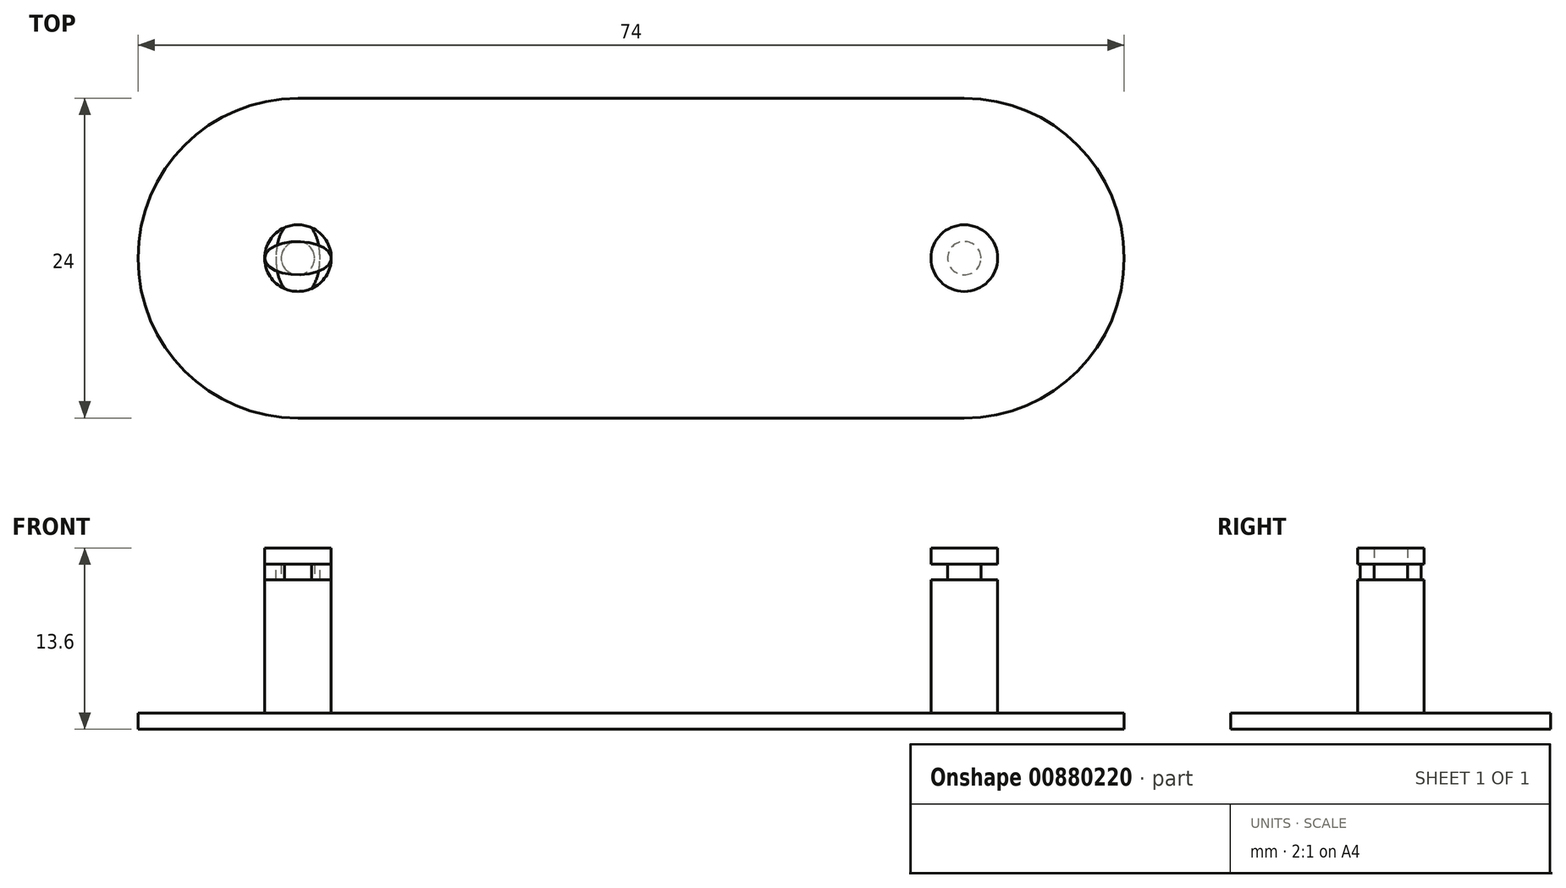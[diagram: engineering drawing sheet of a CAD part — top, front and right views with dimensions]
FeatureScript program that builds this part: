
annotation { "Feature Type Name" : "Feature", "Feature Type Description" : "" }
export const myFeature = defineFeature(function(context is Context, id is Id, definition is map)
    precondition{}
    {
        {
            var Q0;
            Q0=qCreatedBy(makeId("Top.planeOp"),FACE);
            var sketch = newSketch(context, id + "F0", { "sketchPlane" : qUnion([Q0])});
            skLineSegment(sketch, "E0", {"start": v(0, -12) * mm, "end": v(50, -12) * mm});
            skLineSegment(sketch, "E1", {"start": v(0, 12) * mm, "end": v(50, 12) * mm});
            skArc(sketch, "E2", {"start": v(0, -12) * mm, "mid": v(-12, 0) * mm, "end": v(0, 12) * mm});
            skArc(sketch, "E3", {"start": v(50, 12) * mm, "mid": v(62, 0) * mm, "end": v(50, -12) * mm});
            skSolve(sketch);
        }
        {
            var Q0;
            Q0=makeQuery(id+"F0.imprint","IMPRINT",FACE,{"disambiguationData":[TD([[makeQuery(id+"F0.imprint","IMPRINT",EDGE,{"derivedFrom":sQuery(id+"F0.wireOp",EDGE,"E0")}),1.0]])]});
            extrude(context, id + "F1", {"entities" : qUnion([Q0]), "depth" : 1.2 * mm, "offsetDistance" : 25 * mm});
        }
        {
            var Q0;
            Q0=makeQuery(id+"F1.opExtrude","CAP_FACE",FACE,{"disambiguationData":[OSD([sQuery(id+"F0.wireOp",EDGE,"E0"),sQuery(id+"F0.wireOp",EDGE,"E1"),sQuery(id+"F0.wireOp",EDGE,"E2"),sQuery(id+"F0.wireOp",EDGE,"E3")])],"isStart":false});
            var sketch = newSketch(context, id + "F2", { "sketchPlane" : qUnion([Q0])});
            skCircle(sketch, "E4", {"center": v(0, 0) * mm, "radius": 2.5 * mm});
            skCircle(sketch, "E5", {"center": v(50, 0) * mm, "radius": 2.5 * mm});
            skSolve(sketch);
        }
        {
            var Q0;
            Q0 = qSketchRegion(id + "F2", true);
            extrude(context, id + "F3", {"entities" : qUnion([Q0]), "operationType" : NewBodyOperationType.ADD, "depth" : 10 * mm, "offsetDistance" : 25 * mm});
        }
        {
            var Q0;
            Q0=makeQuery(id+"F3.opExtrude","CAP_FACE",FACE,{"disambiguationData":[OSD([sQuery(id+"F2.wireOp",EDGE,"E4")])],"isStart":false});
            var sketch = newSketch(context, id + "F4", { "sketchPlane" : qUnion([Q0])});
            skCircle(sketch, "E6", {"center": v(0, 0) * mm, "radius": 1.25 * mm});
            skSolve(sketch);
        }
        {
            var Q0;
            Q0=makeQuery(id+"F3.opExtrude","CAP_FACE",FACE,{"disambiguationData":[OSD([sQuery(id+"F2.wireOp",EDGE,"E5")])],"isStart":false});
            var sketch = newSketch(context, id + "F5", { "sketchPlane" : qUnion([Q0])});
            skCircle(sketch, "E7", {"center": v(50, 0) * mm, "radius": 1.25 * mm});
            skSolve(sketch);
        }
        {
            var Q0;
            Q0=makeQuery(id+"F4.imprint","IMPRINT",FACE,{"disambiguationData":[TD([[makeQuery(id+"F4.imprint","IMPRINT",EDGE,{"derivedFrom":sQuery(id+"F4.wireOp",EDGE,"E6")}),1.0]])]});
            var Q1;
            Q1=makeQuery(id+"F5.imprint","IMPRINT",FACE,{"disambiguationData":[TD([[makeQuery(id+"F5.imprint","IMPRINT",EDGE,{"derivedFrom":sQuery(id+"F5.wireOp",EDGE,"E7")}),1.0]])]});
            extrude(context, id + "F6", {"entities" : qUnion([Q0, Q1]), "operationType" : NewBodyOperationType.ADD, "depth" : 1.2 * mm, "offsetDistance" : 25 * mm});
        }
        {
            var Q0;
            Q0=makeQuery(id+"F6.opExtrude","CAP_FACE",FACE,{"disambiguationData":[OSD([sQuery(id+"F4.wireOp",EDGE,"E6")])],"isStart":false});
            var sketch = newSketch(context, id + "F7", { "sketchPlane" : qUnion([Q0])});
            skEllipse(sketch, "E8", {"center": v(0, 0) * mm, "majorRadius": 1.25 * mm, "minorRadius": 2.5 * mm, "majorAxis": v(0, 1)});
            skSolve(sketch);
        }
        {
            var Q0;
            Q0=makeQuery(id+"F6.opExtrude","CAP_FACE",FACE,{"disambiguationData":[OSD([sQuery(id+"F5.wireOp",EDGE,"E7")])],"isStart":false});
            var sketch = newSketch(context, id + "F8", { "sketchPlane" : qUnion([Q0])});
            skCircle(sketch, "E9", {"center": v(50, 0) * mm, "radius": 2.5 * mm});
            skSolve(sketch);
        }
        {
            var Q0;
            {var subQ0=sQuery(id+"F7.wireOp",EDGE,"E8");var subQ1=makeQuery(id+"F6.opExtrude","CAP_EDGE",EDGE,{"disambiguationData":[OSD([sQuery(id+"F4.wireOp",EDGE,"E6")])],"isStart":false});var subQ2=makeQuery(id+"F7.imprint","INTERSECT",VERTEX,{"disambiguationData":[OD(0.0)],"derivedFrom":[subQ1,subQ0]});Q0=makeQuery(id+"F7.imprint","IMPRINT",FACE,{"disambiguationData":[TD([[makeQuery(id+"F7.imprint","IMPRINT",EDGE,{"disambiguationData":[TD([[subQ2,1.0]])],"derivedFrom":subQ0}),1.0]])]});}
            var Q1;
            {var subQ0=sQuery(id+"F7.wireOp",EDGE,"E8");var subQ1=makeQuery(id+"F6.opExtrude","CAP_EDGE",EDGE,{"disambiguationData":[OSD([sQuery(id+"F4.wireOp",EDGE,"E6")])],"isStart":false});var subQ2=makeQuery(id+"F7.imprint","INTERSECT",VERTEX,{"disambiguationData":[OD(0.0)],"derivedFrom":[subQ1,subQ0]});Q1=makeQuery(id+"F7.imprint","IMPRINT",FACE,{"disambiguationData":[TD([[makeQuery(id+"F7.imprint","IMPRINT",EDGE,{"disambiguationData":[TD([[subQ2,-1.0]])],"derivedFrom":subQ1}),1.0]])]});}
            var Q2;
            {var subQ0=sQuery(id+"F7.wireOp",EDGE,"E8");var subQ1=makeQuery(id+"F6.opExtrude","CAP_EDGE",EDGE,{"disambiguationData":[OSD([sQuery(id+"F4.wireOp",EDGE,"E6")])],"isStart":false});var subQ2=makeQuery(id+"F7.imprint","INTERSECT",VERTEX,{"disambiguationData":[OD(0.0)],"derivedFrom":[subQ1,subQ0]});Q2=makeQuery(id+"F7.imprint","IMPRINT",FACE,{"disambiguationData":[TD([[makeQuery(id+"F7.imprint","IMPRINT",EDGE,{"disambiguationData":[TD([[subQ2,-1.0]])],"derivedFrom":subQ0}),1.0]])]});}
            var Q3;
            Q3=makeQuery(id+"F8.imprint","IMPRINT",FACE,{"disambiguationData":[TD([[makeQuery(id+"F8.imprint","IMPRINT",EDGE,{"derivedFrom":sQuery(id+"F8.wireOp",EDGE,"E9")}),1.0]])]});
            var Q4;
            Q4=makeQuery(id+"F8.imprint","IMPRINT",FACE,{"disambiguationData":[TD([[makeQuery(id+"F8.imprint","IMPRINT",EDGE,{"derivedFrom":makeQuery(id+"F6.opExtrude","CAP_EDGE",EDGE,{"disambiguationData":[OSD([sQuery(id+"F5.wireOp",EDGE,"E7")])],"isStart":false})}),1.0]])]});
            extrude(context, id + "F9", {"entities" : qUnion([Q0, Q1, Q2, Q3, Q4]), "operationType" : NewBodyOperationType.ADD, "depth" : 1.2 * mm, "offsetDistance" : 25 * mm});
        }
        {
            var Q0;
            Q0=makeQuery(id+"F3.opExtrude","CAP_FACE",FACE,{"disambiguationData":[OSD([sQuery(id+"F2.wireOp",EDGE,"E4")])],"isStart":false});
            var sketch = newSketch(context, id + "F10", { "sketchPlane" : qUnion([Q0])});
            skArc(sketch, "E10.0", {"start": v(0, -12) * mm, "mid": v(-12, 0) * mm, "end": v(0, 12) * mm});
            skLineSegment(sketch, "E11.0", {"start": v(0, -12) * mm, "end": v(50, -12) * mm});
            skEllipse(sketch, "E12", {"center": v(0, 0) * mm, "majorRadius": 1.65 * mm, "minorRadius": 2.9 * mm, "majorAxis": v(1, 0)});
            skArc(sketch, "E13", {"start": v(51.65, 0) * mm, "mid": v(51.3, 6.04) * mm, "end": v(50.24, 12) * mm});
            skArc(sketch, "E14", {"start": v(48.4, -0.4) * mm, "mid": v(50.2, -1.64) * mm, "end": v(51.65, 0) * mm});
            skLineSegment(sketch, "E15", {"start": v(0, 12) * mm, "end": v(46.94, 12) * mm});
            skArc(sketch, "E16", {"start": v(50, -12) * mm, "mid": v(62, -0.12) * mm, "end": v(50.24, 12) * mm});
            skCircle(sketch, "E17.0", {"center": v(50, 0) * mm, "radius": 1.25 * mm, "construction": true});
            skLineSegment(sketch, "E18", {"start": v(48.4, -0.4) * mm, "end": v(46, -0.4) * mm});
            skLineSegment(sketch, "E19", {"start": v(46, -0.4) * mm, "end": v(46, 7.94) * mm});
            skLineSegment(sketch, "E20", {"start": v(46, 7.94) * mm, "end": v(48.35, 0) * mm});
            skArc(sketch, "E21", {"start": v(48.35, 0) * mm, "mid": v(48.83, 1.17) * mm, "end": v(50, 1.65) * mm});
            skLineSegment(sketch, "E22", {"start": v(50, 1.65) * mm, "end": v(46.94, 12) * mm});
            skSolve(sketch);
        }
        {
            var Q0;
            {var subQ11=sQuery(id+"F10.wireOp",EDGE,"E10.0");Q0=makeQuery(id+"F10.imprint","IMPRINT",FACE,{"disambiguationData":[TD([[makeQuery(id+"F10.imprint","IMPRINT",EDGE,{"derivedFrom":subQ11}),-1.0]])]});}
            var Q1;
            {var subQ0=sQuery(id+"F10.wireOp",EDGE,"E12");var subQ1=makeQuery(id+"F3.opExtrude","CAP_EDGE",EDGE,{"disambiguationData":[OSD([sQuery(id+"F2.wireOp",EDGE,"E4")])],"isStart":false});var subQ2=makeQuery(id+"F10.imprint","INTERSECT",VERTEX,{"disambiguationData":[OD(2.0)],"derivedFrom":[subQ1,subQ0]});Q1=makeQuery(id+"F10.imprint","IMPRINT",FACE,{"disambiguationData":[TD([[makeQuery(id+"F10.imprint","IMPRINT",EDGE,{"disambiguationData":[TD([[subQ2,-1.0]])],"derivedFrom":subQ0}),-1.0]])]});}
            var Q2;
            {var subQ0=sQuery(id+"F10.wireOp",EDGE,"E12");var subQ1=makeQuery(id+"F3.opExtrude","CAP_EDGE",EDGE,{"disambiguationData":[OSD([sQuery(id+"F2.wireOp",EDGE,"E4")])],"isStart":false});var subQ2=makeQuery(id+"F10.imprint","INTERSECT",VERTEX,{"disambiguationData":[OD(0.0)],"derivedFrom":[subQ1,subQ0]});Q2=makeQuery(id+"F10.imprint","IMPRINT",FACE,{"disambiguationData":[TD([[makeQuery(id+"F10.imprint","IMPRINT",EDGE,{"disambiguationData":[TD([[subQ2,1.0]])],"derivedFrom":subQ0}),-1.0]])]});}
            extrude(context, id + "F11", {"entities" : qUnion([Q0, Q1, Q2]), "depth" : 1.2 * mm, "offsetDistance" : 25 * mm});
        }
    });
